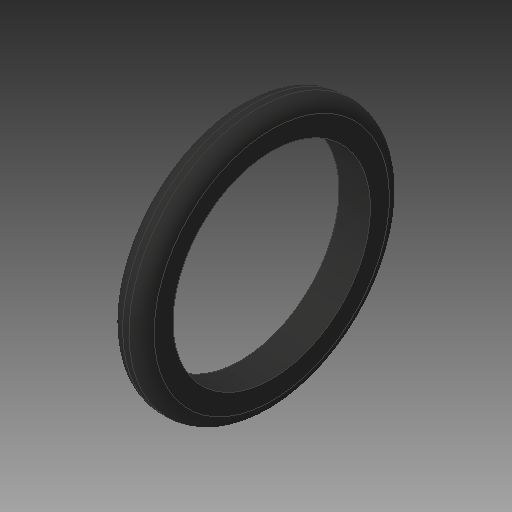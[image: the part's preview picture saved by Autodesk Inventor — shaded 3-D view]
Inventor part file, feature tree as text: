
AUTODESK INVENTOR PART (.ipt)
format: ipt  version: 2019.2 (Build 232265000, 265)  size: 147,456 bytes
history: native  units: mm
features: revolve x1, fillet x1, sketch x1
ambient origin geometry x8: Origin, YZ Plane, XZ Plane, XY Plane, X Axis, Y Axis, Z Axis, Center Point
bodies: Solid1 (feature_tree)
feature tree (3):
  revolve  "Revolution2"  [1 undecoded]
  fillet  "Fillet1"  Radius=75.0mm
  sketch  "Sketch3"  dims[d32=90.0deg d47=30.0mm d48=75.0mm d49=75.0mm d50=310.0mm]
note: 1 required parameter value undecoded (feature->parameter linkage not recoverable at this tier; creation-order binding heuristic only, values carry confidence <= 0.55)
